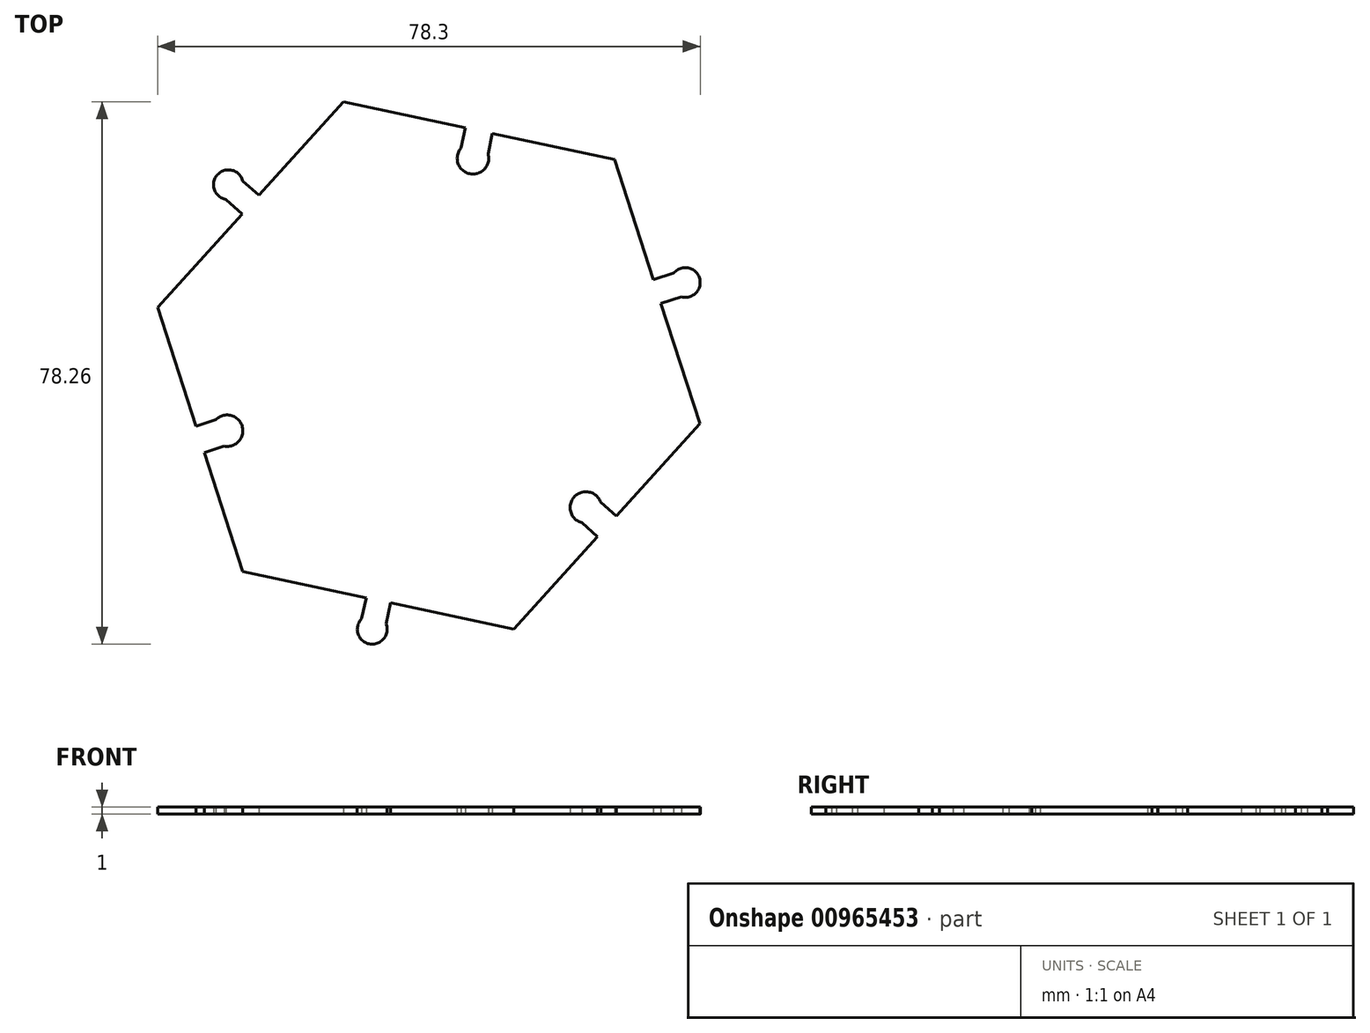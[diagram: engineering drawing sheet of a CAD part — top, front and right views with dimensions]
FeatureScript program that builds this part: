
annotation { "Feature Type Name" : "Feature", "Feature Type Description" : "" }
export const myFeature = defineFeature(function(context is Context, id is Id, definition is map)
    precondition{}
    {
        {
            var Q0;
            Q0=qCreatedBy(makeId("Top.planeOp"),FACE);
            var sketch = newSketch(context, id + "F0", { "sketchPlane" : qUnion([Q0])});
            skCircle(sketch, "E0.cCircle", {"center": v(31.33, -79.95) * mm, "radius": 40 * mm, "construction": true});
            skLineSegment(sketch, "E0.0", {"start": v(70.44, -88.32) * mm, "end": v(58.38, -101.68) * mm});
            skLineSegment(sketch, "E0.1", {"start": v(43.64, -118.01) * mm, "end": v(4.53, -109.65) * mm});
            skLineSegment(sketch, "E0.2", {"start": v(-1.01, -92.52) * mm, "end": v(4.53, -109.65) * mm});
            skLineSegment(sketch, "E0.3", {"start": v(-7.79, -71.59) * mm, "end": v(19.02, -41.9) * mm});
            skLineSegment(sketch, "E0.4", {"start": v(19.02, -41.9) * mm, "end": v(36.62, -45.66) * mm});
            skLineSegment(sketch, "E0.5", {"start": v(70.44, -88.32) * mm, "end": v(58.13, -50.26) * mm});
            skLineSegment(sketch, "E1", {"start": v(2.25, -89.36) * mm, "end": v(-1.63, -90.62) * mm, "construction": true});
            skLineSegment(sketch, "E2.0", {"start": v(0.6, -87.8) * mm, "end": v(-2.25, -88.71) * mm});
            skLineSegment(sketch, "E3.0", {"start": v(1.84, -91.6) * mm, "end": v(-1.01, -92.52) * mm});
            skArc(sketch, "E4", {"start": v(1.84, -91.6) * mm, "mid": v(4.41, -88.66) * mm, "end": v(0.6, -87.8) * mm});
            skLineSegment(sketch, "E5", {"start": v(37.72, -50.07) * mm, "end": v(38.58, -46.08) * mm, "construction": true});
            skLineSegment(sketch, "E6.0", {"start": v(39.9, -49.43) * mm, "end": v(40.53, -46.5) * mm});
            skLineSegment(sketch, "E7.0", {"start": v(36, -48.6) * mm, "end": v(36.62, -45.66) * mm});
            skArc(sketch, "E8", {"start": v(36, -48.6) * mm, "mid": v(37.25, -52.29) * mm, "end": v(39.9, -49.43) * mm});
            skLineSegment(sketch, "E9", {"start": v(54.02, -100.44) * mm, "end": v(57.04, -103.17) * mm, "construction": true});
            skLineSegment(sketch, "E10.0", {"start": v(53.48, -102.64) * mm, "end": v(55.7, -104.65) * mm});
            skLineSegment(sketch, "E11.0", {"start": v(56.16, -99.67) * mm, "end": v(58.38, -101.68) * mm});
            skArc(sketch, "E12", {"start": v(56.16, -99.67) * mm, "mid": v(52.33, -98.91) * mm, "end": v(53.48, -102.64) * mm});
            skLineSegment(sketch, "E13", {"start": v(2.44, -53.88) * mm, "end": v(5.62, -56.74) * mm, "construction": true});
            skLineSegment(sketch, "E14.0", {"start": v(2.1, -56) * mm, "end": v(4.41, -58.08) * mm});
            skLineSegment(sketch, "E15.0", {"start": v(4.52, -53.33) * mm, "end": v(6.82, -55.4) * mm});
            skLineSegment(sketch, "E16", {"start": v(4.41, -58.08) * mm, "end": v(6.82, -55.4) * mm, "construction": true});
            skCircle(sketch, "E17", {"center": v(2.44, -53.88) * mm, "radius": 2.15 * mm});
            skLineSegment(sketch, "E18", {"start": v(4.52, -53.33) * mm, "end": v(2.1, -56) * mm, "construction": true});
            skLineSegment(sketch, "E19", {"start": v(23.19, -118.01) * mm, "end": v(24.08, -113.83) * mm, "construction": true});
            skLineSegment(sketch, "E20.0", {"start": v(25.2, -117.24) * mm, "end": v(25.84, -114.2) * mm});
            skLineSegment(sketch, "E21.0", {"start": v(21.68, -116.48) * mm, "end": v(22.32, -113.45) * mm});
            skLineSegment(sketch, "E22", {"start": v(25.84, -114.2) * mm, "end": v(22.32, -113.45) * mm, "construction": true});
            skCircle(sketch, "E23", {"center": v(23.19, -118.01) * mm, "radius": 2.15 * mm});
            skLineSegment(sketch, "E24", {"start": v(21.68, -116.48) * mm, "end": v(25.2, -117.24) * mm, "construction": true});
            skLineSegment(sketch, "E25", {"start": v(68.36, -67.98) * mm, "end": v(64.29, -69.3) * mm, "construction": true});
            skLineSegment(sketch, "E26.0", {"start": v(66.68, -66.63) * mm, "end": v(63.74, -67.58) * mm});
            skLineSegment(sketch, "E27.0", {"start": v(67.8, -70.05) * mm, "end": v(64.84, -71) * mm});
            skLineSegment(sketch, "E28", {"start": v(63.74, -67.58) * mm, "end": v(64.84, -71) * mm, "construction": true});
            skCircle(sketch, "E29", {"center": v(68.36, -67.98) * mm, "radius": 2.15 * mm});
            skLineSegment(sketch, "E30", {"start": v(67.8, -70.05) * mm, "end": v(66.68, -66.63) * mm, "construction": true});
            skLineSegment(sketch, "E31.trimOffspring", {"start": v(-7.79, -71.59) * mm, "end": v(-2.25, -88.71) * mm});
            skLineSegment(sketch, "E32.trimOffspring", {"start": v(40.53, -46.5) * mm, "end": v(58.13, -50.26) * mm});
            skLineSegment(sketch, "E33.trimOffspring", {"start": v(55.7, -104.65) * mm, "end": v(43.64, -118.01) * mm});
            skLineSegment(sketch, "E34", {"start": v(36, -48.6) * mm, "end": v(39.9, -49.43) * mm, "construction": true});
            skSolve(sketch);
        }
        {
            var Q0;
            {var subQ10=sQuery(id+"F0.wireOp",EDGE,"E0.0");Q0=makeQuery(id+"F0.imprint","IMPRINT",FACE,{"disambiguationData":[TD([[makeQuery(id+"F0.imprint","IMPRINT",EDGE,{"derivedFrom":subQ10}),-1.0]])]});}
            var Q1;
            {var subQ0=sQuery(id+"F0.wireOp",EDGE,"E14.0");Q1=makeQuery(id+"F0.imprint","IMPRINT",FACE,{"disambiguationData":[TD([[makeQuery(id+"F0.imprint","IMPRINT",EDGE,{"derivedFrom":subQ0}),1.0]])]});}
            var Q2;
            {var subQ0=sQuery(id+"F0.wireOp",EDGE,"E17");var subQ1=makeQuery(id+"F0.imprint","INTERSECT",VERTEX,{"derivedFrom":[sQuery(id+"F0.wireOp",EDGE,"E14.0"),subQ0]});Q2=makeQuery(id+"F0.imprint","IMPRINT",FACE,{"disambiguationData":[TD([[makeQuery(id+"F0.imprint","IMPRINT",EDGE,{"disambiguationData":[TD([[subQ1,1.0]])],"derivedFrom":subQ0}),1.0]])]});}
            var Q3;
            {var subQ0=sQuery(id+"F0.wireOp",EDGE,"E29");var subQ1=makeQuery(id+"F0.imprint","INTERSECT",VERTEX,{"derivedFrom":[sQuery(id+"F0.wireOp",EDGE,"E26.0"),subQ0]});Q3=makeQuery(id+"F0.imprint","IMPRINT",FACE,{"disambiguationData":[TD([[makeQuery(id+"F0.imprint","IMPRINT",EDGE,{"disambiguationData":[TD([[subQ1,1.0]])],"derivedFrom":subQ0}),1.0]])]});}
            var Q4;
            {var subQ0=sQuery(id+"F0.wireOp",EDGE,"E26.0");Q4=makeQuery(id+"F0.imprint","IMPRINT",FACE,{"disambiguationData":[TD([[makeQuery(id+"F0.imprint","IMPRINT",EDGE,{"derivedFrom":subQ0}),1.0]])]});}
            var Q5;
            {var subQ0=sQuery(id+"F0.wireOp",EDGE,"E20.0");Q5=makeQuery(id+"F0.imprint","IMPRINT",FACE,{"disambiguationData":[TD([[makeQuery(id+"F0.imprint","IMPRINT",EDGE,{"derivedFrom":subQ0}),1.0]])]});}
            var Q6;
            {var subQ0=sQuery(id+"F0.wireOp",EDGE,"E23");var subQ1=makeQuery(id+"F0.imprint","INTERSECT",VERTEX,{"derivedFrom":[sQuery(id+"F0.wireOp",EDGE,"E20.0"),subQ0]});Q6=makeQuery(id+"F0.imprint","IMPRINT",FACE,{"disambiguationData":[TD([[makeQuery(id+"F0.imprint","IMPRINT",EDGE,{"disambiguationData":[TD([[subQ1,1.0]])],"derivedFrom":subQ0}),1.0]])]});}
            extrude(context, id + "F1", {"entities" : qUnion([Q0, Q1, Q2, Q3, Q4, Q5, Q6]), "depth" : 1 * mm, "offsetDistance" : 25 * mm});
        }
    });
